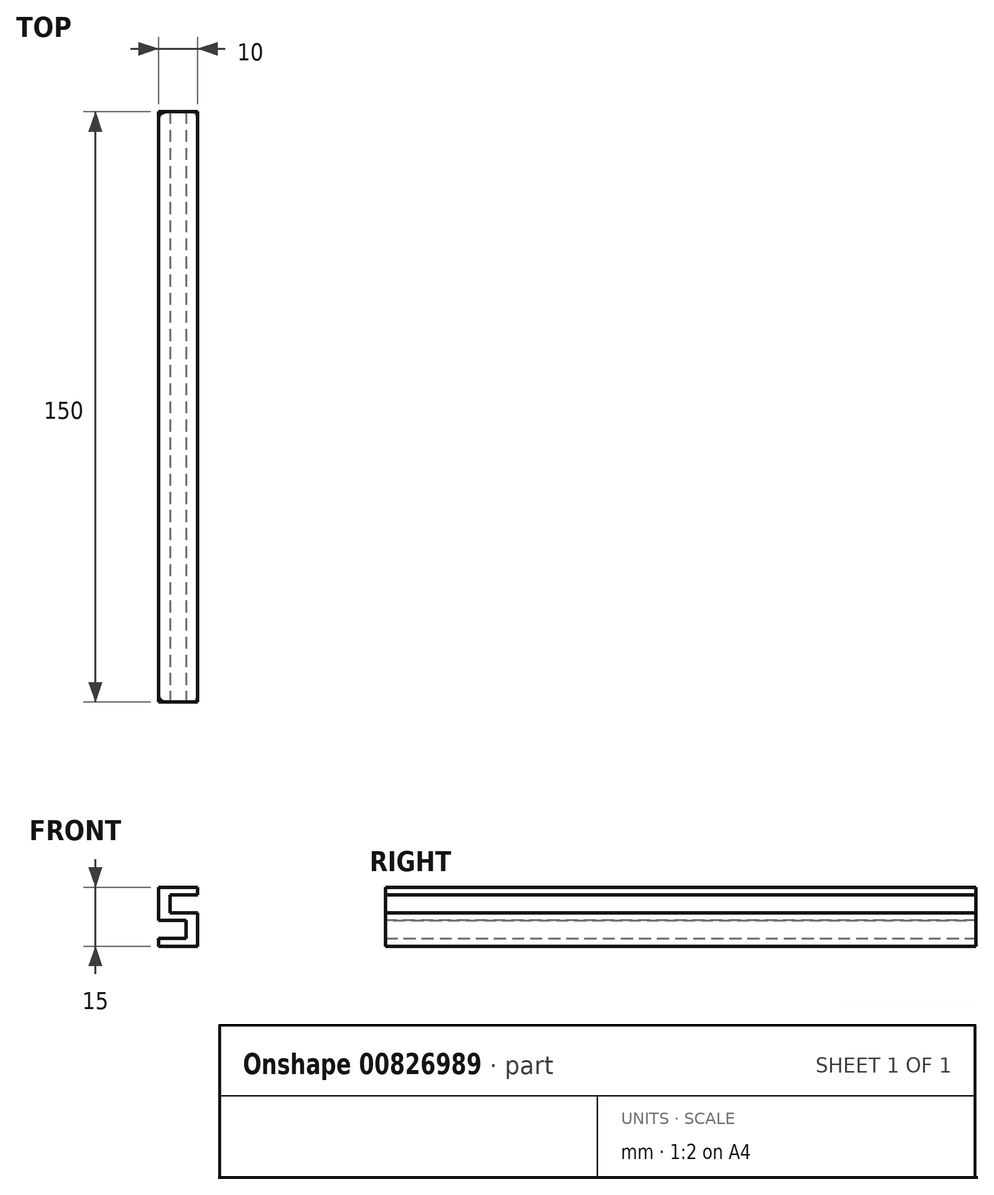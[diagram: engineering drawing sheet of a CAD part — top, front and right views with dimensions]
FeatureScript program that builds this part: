
annotation { "Feature Type Name" : "Feature", "Feature Type Description" : "" }
export const myFeature = defineFeature(function(context is Context, id is Id, definition is map)
    precondition{}
    {
        {
            var Q0;
            Q0=qCreatedBy(makeId("Top.planeOp"),FACE);
            var sketch = newSketch(context, id + "F0", { "sketchPlane" : qUnion([Q0])});
            skLineSegment(sketch, "E0.bottom", {"start": v(5, -75) * mm, "end": v(-5, -75) * mm});
            skLineSegment(sketch, "E0.top", {"start": v(5, 75) * mm, "end": v(-5, 75) * mm});
            skLineSegment(sketch, "E0.left", {"start": v(5, -75) * mm, "end": v(5, 75) * mm});
            skLineSegment(sketch, "E0.right", {"start": v(-5, -75) * mm, "end": v(-5, 75) * mm});
            skPoint(sketch, "E0.middle", {"position": v(0, 0) * mm});
            skSolve(sketch);
        }
        {
            var Q0;
            Q0=qSketchRegion(id+"F0",true);
            extrude(context, id + "F1", {"entities" : qUnion([Q0]), "depth" : 2 * mm, "offsetDistance" : 25 * mm});
        }
        {
            var Q0;
            Q0=makeQuery(id+"F1.opExtrude","CAP_FACE",FACE,{"disambiguationData":[OSD([sQuery(id+"F0.wireOp",EDGE,"E0.bottom"),sQuery(id+"F0.wireOp",EDGE,"E0.top"),sQuery(id+"F0.wireOp",EDGE,"E0.left"),sQuery(id+"F0.wireOp",EDGE,"E0.right")])],"isStart":false});
            var sketch = newSketch(context, id + "F2", { "sketchPlane" : qUnion([Q0])});
            skLineSegment(sketch, "E1.bottom", {"start": v(5, 75) * mm, "end": v(2, 75) * mm});
            skLineSegment(sketch, "E1.top", {"start": v(5, -75) * mm, "end": v(2, -75) * mm});
            skLineSegment(sketch, "E1.left", {"start": v(5, 75) * mm, "end": v(5, -75) * mm});
            skLineSegment(sketch, "E1.right", {"start": v(2, 75) * mm, "end": v(2, -75) * mm});
            skSolve(sketch);
        }
        {
            var Q0;
            Q0=makeQuery(id+"F2.imprint","IMPRINT",FACE,{"disambiguationData":[TD([[makeQuery(id+"F2.imprint","IMPRINT",EDGE,{"derivedFrom":sQuery(id+"F2.wireOp",EDGE,"E1.bottom")}),1.0]])]});
            var Q1;
            Q1=makeQuery(id+"F2.imprint","IMPRINT",FACE,{"disambiguationData":[TD([[makeQuery(id+"F2.imprint","IMPRINT",EDGE,{"derivedFrom":sQuery(id+"F2.wireOp",EDGE,"TBBfLngB-xCYf-ifmG-CJWj-5pNpHj6gDzCJ.bottom")}),1.0]])]});
            extrude(context, id + "F3", {"entities" : qUnion([Q0, Q1]), "operationType" : NewBodyOperationType.ADD, "depth" : 4.5 * mm, "offsetDistance" : 25 * mm});
        }
        {
            var Q0;
            Q0=makeQuery(id+"F3.opExtrude","CAP_FACE",FACE,{"disambiguationData":[OSD([sQuery(id+"F2.wireOp",EDGE,"E1.bottom"),sQuery(id+"F2.wireOp",EDGE,"E1.top"),sQuery(id+"F2.wireOp",EDGE,"E1.left"),sQuery(id+"F2.wireOp",EDGE,"E1.right"),sQuery(id+"F2.wireOp",EDGE,"TBBfLngB-xCYf-ifmG-CJWj-5pNpHj6gDzCJ.bottom"),sQuery(id+"F2.wireOp",EDGE,"TBBfLngB-xCYf-ifmG-CJWj-5pNpHj6gDzCJ.top"),sQuery(id+"F2.wireOp",EDGE,"TBBfLngB-xCYf-ifmG-CJWj-5pNpHj6gDzCJ.right")])],"isStart":false});
            var sketch = newSketch(context, id + "F4", { "sketchPlane" : qUnion([Q0])});
            skLineSegment(sketch, "E2.bottom", {"start": v(-5, -75) * mm, "end": v(5, -75) * mm});
            skLineSegment(sketch, "E2.top", {"start": v(-5, 75) * mm, "end": v(5, 75) * mm});
            skLineSegment(sketch, "E2.left", {"start": v(-5, -75) * mm, "end": v(-5, 75) * mm});
            skLineSegment(sketch, "E2.right", {"start": v(5, -75) * mm, "end": v(5, 75) * mm});
            skSolve(sketch);
        }
        {
            var Q0;
            {var subQ0=sQuery(id+"F4.wireOp",EDGE,"E2.right");Q0=makeQuery(id+"F4.imprint","IMPRINT",FACE,{"disambiguationData":[TD([[makeQuery(id+"F4.imprint","IMPRINT",EDGE,{"derivedFrom":subQ0}),1.0]])]});}
            var Q1;
            {var subQ0=sQuery(id+"F4.wireOp",EDGE,"E2.left");Q1=makeQuery(id+"F4.imprint","IMPRINT",FACE,{"disambiguationData":[TD([[makeQuery(id+"F4.imprint","IMPRINT",EDGE,{"derivedFrom":subQ0}),-1.0]])]});}
            var Q2;
            {var subQ1=sQuery(id+"F4.wireOp",EDGE,"KL0TRBLz-bGL5-0MkN-P1Di-jsCCVjPQuZuJ.bottom");Q2=makeQuery(id+"F4.imprint","IMPRINT",FACE,{"disambiguationData":[TD([[makeQuery(id+"F4.imprint","IMPRINT",EDGE,{"derivedFrom":subQ1}),-1.0]])]});}
            var Q3;
            {var subQ6=sQuery(id+"F4.wireOp",EDGE,"KL0TRBLz-bGL5-0MkN-P1Di-jsCCVjPQuZuJ.top");Q3=makeQuery(id+"F4.imprint","IMPRINT",FACE,{"disambiguationData":[TD([[makeQuery(id+"F4.imprint","IMPRINT",EDGE,{"derivedFrom":subQ6}),-1.0]])]});}
            extrude(context, id + "F5", {"entities" : qUnion([Q0, Q1, Q2, Q3]), "operationType" : NewBodyOperationType.ADD, "depth" : 2 * mm, "offsetDistance" : 25 * mm});
        }
        {
            var Q0;
            Q0=makeQuery(id+"F5.opExtrude","CAP_FACE",FACE,{"disambiguationData":[OSD([sQuery(id+"F4.wireOp",EDGE,"KL0TRBLz-bGL5-0MkN-P1Di-jsCCVjPQuZuJ.bottom"),sQuery(id+"F4.wireOp",EDGE,"KL0TRBLz-bGL5-0MkN-P1Di-jsCCVjPQuZuJ.top"),sQuery(id+"F4.wireOp",EDGE,"KL0TRBLz-bGL5-0MkN-P1Di-jsCCVjPQuZuJ.left"),sQuery(id+"F4.wireOp",EDGE,"KL0TRBLz-bGL5-0MkN-P1Di-jsCCVjPQuZuJ.right"),sQuery(id+"F4.wireOp",EDGE,"E2.top"),sQuery(id+"F4.wireOp",EDGE,"E2.left"),sQuery(id+"F4.wireOp",EDGE,"E2.right")])],"isStart":false});
            var sketch = newSketch(context, id + "F6", { "sketchPlane" : qUnion([Q0])});
            skLineSegment(sketch, "E3.bottom", {"start": v(-5, 75) * mm, "end": v(-2, 75) * mm});
            skLineSegment(sketch, "E3.left", {"start": v(-5, 75) * mm, "end": v(-5, -75) * mm});
            skLineSegment(sketch, "E3.right", {"start": v(-2, 75) * mm, "end": v(-2, -75) * mm});
            skSolve(sketch);
        }
        {
            var Q0;
            Q0=makeQuery(id+"F6.imprint","IMPRINT",FACE,{"disambiguationData":[TD([[makeQuery(id+"F6.imprint","IMPRINT",EDGE,{"derivedFrom":sQuery(id+"F6.wireOp",EDGE,"E3.bottom")}),1.0]])]});
            var Q1;
            Q1=makeQuery(id+"F6.imprint","IMPRINT",FACE,{"disambiguationData":[TD([[makeQuery(id+"F6.imprint","IMPRINT",EDGE,{"derivedFrom":sQuery(id+"F6.wireOp",EDGE,"29kaHYbN-9uL8-V3Mp-fecK-EEq72wYlOBmd.bottom")}),-1.0]])]});
            extrude(context, id + "F7", {"entities" : qUnion([Q0, Q1]), "operationType" : NewBodyOperationType.ADD, "depth" : 4.5 * mm, "offsetDistance" : 25 * mm});
        }
        {
            var Q0;
            Q0=makeQuery(id+"F7.opExtrude","CAP_FACE",FACE,{"disambiguationData":[OSD([sQuery(id+"F6.wireOp",EDGE,"E3.bottom"),sQuery(id+"F6.wireOp",EDGE,"E3.top"),sQuery(id+"F6.wireOp",EDGE,"E3.left"),sQuery(id+"F6.wireOp",EDGE,"E3.right"),sQuery(id+"F6.wireOp",EDGE,"29kaHYbN-9uL8-V3Mp-fecK-EEq72wYlOBmd.bottom"),sQuery(id+"F6.wireOp",EDGE,"29kaHYbN-9uL8-V3Mp-fecK-EEq72wYlOBmd.top"),sQuery(id+"F6.wireOp",EDGE,"29kaHYbN-9uL8-V3Mp-fecK-EEq72wYlOBmd.right")])],"isStart":false});
            var sketch = newSketch(context, id + "F8", { "sketchPlane" : qUnion([Q0])});
            skLineSegment(sketch, "E4.bottom", {"start": v(-5, 75) * mm, "end": v(5, 75) * mm});
            skLineSegment(sketch, "E4.top", {"start": v(-5, -75) * mm, "end": v(5, -75) * mm});
            skLineSegment(sketch, "E4.left", {"start": v(-5, 75) * mm, "end": v(-5, -75) * mm});
            skLineSegment(sketch, "E4.right", {"start": v(5, 75) * mm, "end": v(5, -75) * mm});
            skSolve(sketch);
        }
        {
            var Q0;
            {var subQ2=sQuery(id+"F8.wireOp",EDGE,"E4.top");Q0=makeQuery(id+"F8.imprint","IMPRINT",FACE,{"disambiguationData":[TD([[makeQuery(id+"F8.imprint","IMPRINT",EDGE,{"derivedFrom":subQ2}),-1.0]])]});}
            var Q1;
            {var subQ2=sQuery(id+"F8.wireOp",EDGE,"E4.right");Q1=makeQuery(id+"F8.imprint","IMPRINT",FACE,{"disambiguationData":[TD([[makeQuery(id+"F8.imprint","IMPRINT",EDGE,{"derivedFrom":subQ2}),-1.0]])]});}
            var Q2;
            {var subQ0=sQuery(id+"F8.wireOp",EDGE,"QwVzRym9-oMMP-w3yy-Uq35-inyoNm8EllKR.top");Q2=makeQuery(id+"F8.imprint","IMPRINT",FACE,{"disambiguationData":[TD([[makeQuery(id+"F8.imprint","IMPRINT",EDGE,{"derivedFrom":subQ0}),-1.0]])]});}
            var Q3;
            {var subQ0=sQuery(id+"F8.wireOp",EDGE,"QwVzRym9-oMMP-w3yy-Uq35-inyoNm8EllKR.bottom");Q3=makeQuery(id+"F8.imprint","IMPRINT",FACE,{"disambiguationData":[TD([[makeQuery(id+"F8.imprint","IMPRINT",EDGE,{"derivedFrom":subQ0}),-1.0]])]});}
            extrude(context, id + "F9", {"entities" : qUnion([Q0, Q1, Q2, Q3]), "operationType" : NewBodyOperationType.ADD, "depth" : 2 * mm, "offsetDistance" : 25 * mm});
        }
        {
            var Q0;
            Q0=makeQuery(id+"F9.boolean.opBoolean","MERGE",EDGE,{"derivedFrom":[makeQuery(id+"F7.boolean.opBoolean","MERGE",EDGE,{"derivedFrom":[makeQuery(id+"F5.opExtrude","SWEPT_EDGE",EDGE,{"disambiguationData":[OSD([sQuery(id+"F4.wireOp",EDGE,"E2.top"),sQuery(id+"F4.wireOp",EDGE,"E2.left")])]}),makeQuery(id+"F7.opExtrude","SWEPT_EDGE",EDGE,{"disambiguationData":[OSD([sQuery(id+"F6.wireOp",EDGE,"E3.bottom"),sQuery(id+"F6.wireOp",EDGE,"E3.left")])]})]}),makeQuery(id+"F9.opExtrude","SWEPT_EDGE",EDGE,{"disambiguationData":[OSD([sQuery(id+"F8.wireOp",EDGE,"E4.bottom"),sQuery(id+"F8.wireOp",EDGE,"E4.left")])]})]});
            var Q1;
            Q1=makeQuery(id+"F5.boolean.opBoolean","MERGE",EDGE,{"derivedFrom":[makeQuery(id+"F3.boolean.opBoolean","MERGE",EDGE,{"derivedFrom":[makeQuery(id+"F1.opExtrude","SWEPT_EDGE",EDGE,{"disambiguationData":[OSD([sQuery(id+"F0.wireOp",EDGE,"E0.top"),sQuery(id+"F0.wireOp",EDGE,"E0.left")])]}),makeQuery(id+"F3.opExtrude","SWEPT_EDGE",EDGE,{"disambiguationData":[OSD([sQuery(id+"F2.wireOp",EDGE,"E1.bottom"),sQuery(id+"F2.wireOp",EDGE,"E1.left")])]})]}),makeQuery(id+"F5.opExtrude","SWEPT_EDGE",EDGE,{"disambiguationData":[OSD([sQuery(id+"F4.wireOp",EDGE,"E2.top"),sQuery(id+"F4.wireOp",EDGE,"E2.right")])]})]});
            var Q2;
            {var subQ0=sQuery(id+"F4.wireOp",EDGE,"E2.bottom");Q2=makeQuery(id+"F9.boolean.opBoolean","MERGE",EDGE,{"derivedFrom":[makeQuery(id+"F7.boolean.opBoolean","MERGE",EDGE,{"derivedFrom":[makeQuery(id+"F5.opExtrude","SWEPT_EDGE",EDGE,{"disambiguationData":[OSD([subQ0,sQuery(id+"F4.wireOp",EDGE,"E2.left")])]}),makeQuery(id+"F7.opExtrude","SWEPT_EDGE",EDGE,{"disambiguationData":[OSD([subQ0,sQuery(id+"F6.wireOp",EDGE,"E3.left")])]})]}),makeQuery(id+"F9.opExtrude","SWEPT_EDGE",EDGE,{"disambiguationData":[OSD([sQuery(id+"F8.wireOp",EDGE,"E4.top"),sQuery(id+"F8.wireOp",EDGE,"E4.left")])]})]});}
            var Q3;
            Q3=makeQuery(id+"F5.boolean.opBoolean","MERGE",EDGE,{"derivedFrom":[makeQuery(id+"F3.boolean.opBoolean","MERGE",EDGE,{"derivedFrom":[makeQuery(id+"F1.opExtrude","SWEPT_EDGE",EDGE,{"disambiguationData":[OSD([sQuery(id+"F0.wireOp",EDGE,"E0.bottom"),sQuery(id+"F0.wireOp",EDGE,"E0.left")])]}),makeQuery(id+"F3.opExtrude","SWEPT_EDGE",EDGE,{"disambiguationData":[OSD([sQuery(id+"F2.wireOp",EDGE,"E1.top"),sQuery(id+"F2.wireOp",EDGE,"E1.left")])]})]}),makeQuery(id+"F5.opExtrude","SWEPT_EDGE",EDGE,{"disambiguationData":[OSD([sQuery(id+"F4.wireOp",EDGE,"E2.bottom"),sQuery(id+"F4.wireOp",EDGE,"E2.right")])]})]});
            fillet(context, id + "F10", {"entities" : qUnion([Q0, Q1, Q2, Q3]), "radius" : 2 * mm, "tangentPropagation" : true, "allowEdgeOverflow" : false});
        }
    });
